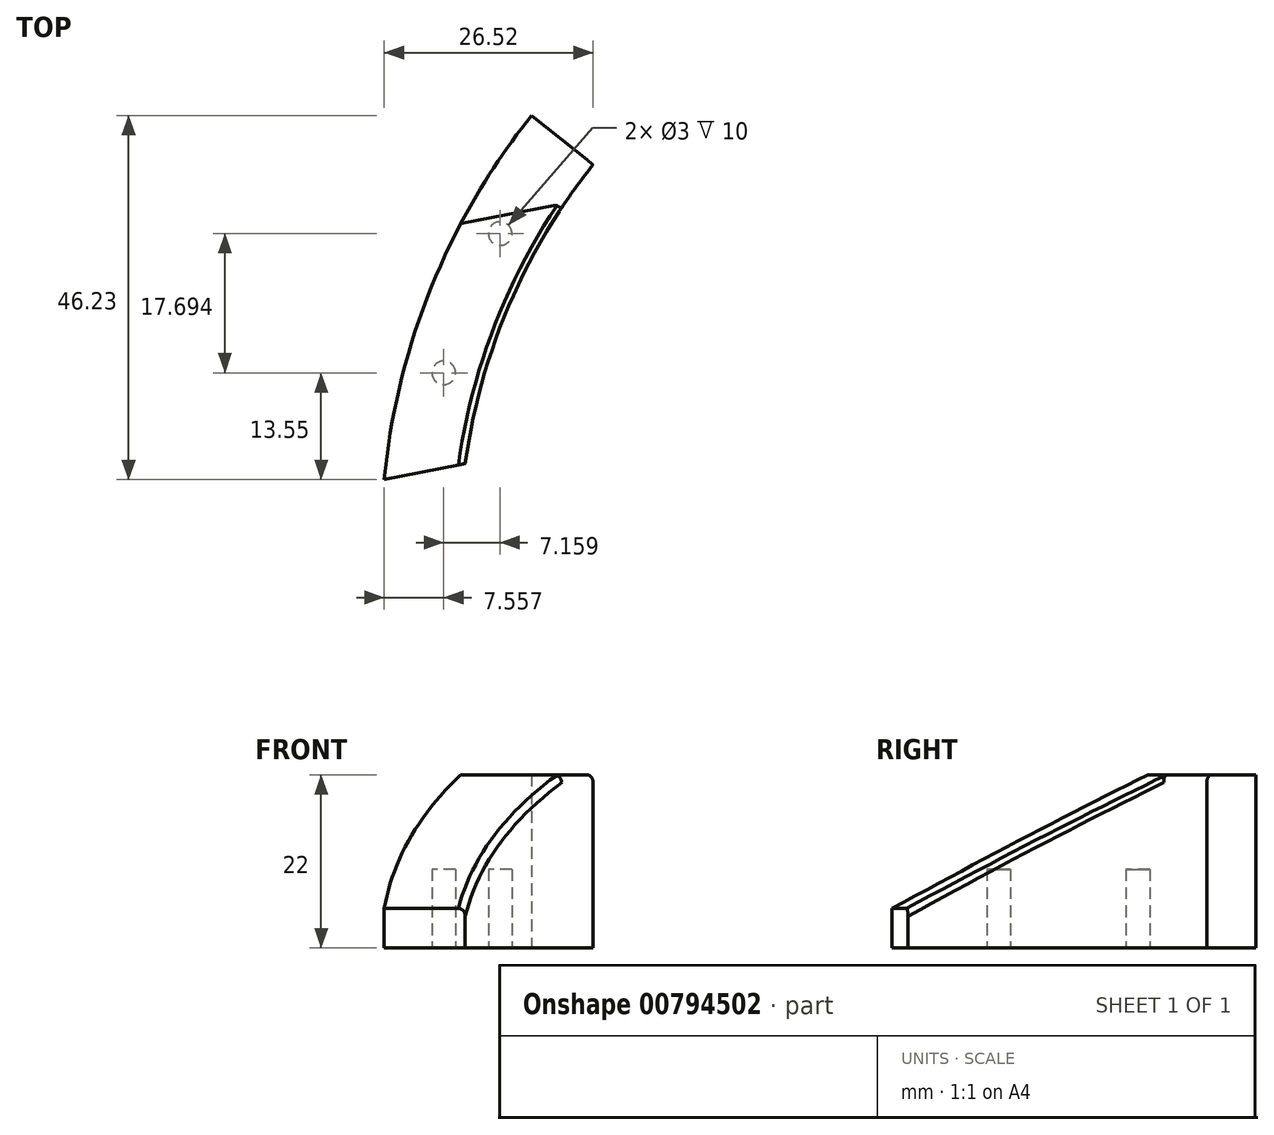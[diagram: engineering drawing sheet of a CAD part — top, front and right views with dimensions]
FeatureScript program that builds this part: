
annotation { "Feature Type Name" : "Feature", "Feature Type Description" : "" }
export const myFeature = defineFeature(function(context is Context, id is Id, definition is map)
    precondition{}
    {
        {
            var Q0;
            Q0=qCreatedBy(makeId("Top.planeOp"),FACE);
            var sketch = newSketch(context, id + "F0", { "sketchPlane" : qUnion([Q0])});
            skCircle(sketch, "E0", {"center": v(0, 0) * mm, "radius": 77.5 * mm});
            skCircle(sketch, "E1", {"center": v(0, 0) * mm, "radius": 76 * mm});
            skCircle(sketch, "E2", {"center": v(0, 0) * mm, "radius": 2.5 * mm});
            skLineSegment(sketch, "E3.bottom", {"start": v(0, 60) * mm, "end": v(-100, 60) * mm, "construction": true});
            skLineSegment(sketch, "E3.top", {"start": v(0, -60) * mm, "end": v(-100, -60) * mm, "construction": true});
            skLineSegment(sketch, "E3.left", {"start": v(0, 60) * mm, "end": v(0, -60) * mm, "construction": true});
            skLineSegment(sketch, "E3.right", {"start": v(-100, 60) * mm, "end": v(-100, -60) * mm, "construction": true});
            skCircle(sketch, "E4", {"center": v(0, 0) * mm, "radius": 87.5 * mm});
            skCircle(sketch, "E5", {"center": v(0, 0) * mm, "radius": 62.5 * mm});
            skLineSegment(sketch, "E6", {"start": v(0, 0) * mm, "end": v(-78.23, -94.42) * mm, "construction": true});
            skLineSegment(sketch, "E7", {"start": v(0, 0) * mm, "end": v(-84.15, 101.51) * mm, "construction": true});
            skLineSegment(sketch, "E8", {"start": v(0, 0) * mm, "end": v(-134.5, -26.47) * mm, "construction": true});
            skLineSegment(sketch, "E9", {"start": v(-85.85, -16.9) * mm, "end": v(-90.68, 7.63) * mm});
            skLineSegment(sketch, "E10", {"start": v(-90.68, 7.63) * mm, "end": v(-31.8, 19.22) * mm});
            skLineSegment(sketch, "E11", {"start": v(-31.8, 19.22) * mm, "end": v(-22.16, -29.84) * mm});
            skLineSegment(sketch, "E12", {"start": v(-22.16, -29.84) * mm, "end": v(-81.03, -41.42) * mm});
            skLineSegment(sketch, "E13", {"start": v(-90.68, 7.63) * mm, "end": v(-81.03, -41.42) * mm});
            skLineSegment(sketch, "E14.0", {"start": v(-84.8, 3.7) * mm, "end": v(-35.75, 13.35) * mm});
            skLineSegment(sketch, "E14.1", {"start": v(-84.8, 3.7) * mm, "end": v(-77.09, -35.55) * mm});
            skLineSegment(sketch, "E14.2", {"start": v(-28.03, -25.9) * mm, "end": v(-77.09, -35.55) * mm});
            skLineSegment(sketch, "E14.3", {"start": v(-35.75, 13.35) * mm, "end": v(-28.03, -25.9) * mm});
            skLineSegment(sketch, "E15.0", {"start": v(-94.2, 10) * mm, "end": v(-29.45, 22.74) * mm});
            skLineSegment(sketch, "E15.1", {"start": v(-94.2, 10) * mm, "end": v(-83.4, -44.95) * mm});
            skLineSegment(sketch, "E15.2", {"start": v(-18.63, -32.2) * mm, "end": v(-83.4, -44.95) * mm});
            skLineSegment(sketch, "E15.3", {"start": v(-29.45, 22.74) * mm, "end": v(-18.63, -32.2) * mm});
            skLineSegment(sketch, "E16", {"start": v(0, 0) * mm, "end": v(-75.25, 10.67) * mm, "construction": true});
            skLineSegment(sketch, "E17", {"start": v(-75.25, 10.67) * mm, "end": v(-86.63, 12.29) * mm});
            skLineSegment(sketch, "E18", {"start": v(-55.84, 67.36) * mm, "end": v(-48.5, 58.5) * mm});
            skLineSegment(sketch, "E19", {"start": v(0, 0) * mm, "end": v(-95.1, 63.54) * mm, "construction": true});
            skLineSegment(sketch, "E20", {"start": v(-72.76, 48.6) * mm, "end": v(-64.44, 43.05) * mm});
            skLineSegment(sketch, "E21", {"start": v(0, 0) * mm, "end": v(-81.95, 67.9) * mm, "construction": true});
            skLineSegment(sketch, "E22", {"start": v(-67.38, 55.83) * mm, "end": v(-59.68, 49.45) * mm});
            skLineSegment(sketch, "E23", {"start": v(0, 0) * mm, "end": v(-87.56, 69.86) * mm, "construction": true});
            skLineSegment(sketch, "E24", {"start": v(-60.58, 48.34) * mm, "end": v(-68.4, 54.57) * mm});
            skCircle(sketch, "E25", {"center": v(0, 0) * mm, "radius": 82.5 * mm, "construction": true});
            skCircle(sketch, "E26", {"center": v(-72.38, 39.58) * mm, "radius": 1.5 * mm});
            skCircle(sketch, "E27", {"center": v(-79.54, 21.89) * mm, "radius": 1.5 * mm});
            skSolve(sketch);
        }
        {
            var Q0;
            {var subQ0=sQuery(id+"F0.wireOp",EDGE,"E15.0");var subQ1=sQuery(id+"F0.wireOp",EDGE,"E0");var subQ2=makeQuery(id+"F0.imprint","INTERSECT",VERTEX,{"derivedFrom":[subQ1,subQ0]});Q0=makeQuery(id+"F0.imprint","IMPRINT",FACE,{"disambiguationData":[TD([[makeQuery(id+"F0.imprint","IMPRINT",EDGE,{"disambiguationData":[TD([[subQ2,-1.0]])],"derivedFrom":subQ1}),-1.0]])]});}
            var Q1;
            {var subQ5=sQuery(id+"F0.wireOp",EDGE,"E20");Q1=makeQuery(id+"F0.imprint","IMPRINT",FACE,{"disambiguationData":[TD([[makeQuery(id+"F0.imprint","IMPRINT",EDGE,{"derivedFrom":subQ5}),-1.0]])]});}
            var Q2;
            {var subQ0=sQuery(id+"F0.wireOp",EDGE,"E20");Q2=makeQuery(id+"F0.imprint","IMPRINT",FACE,{"disambiguationData":[TD([[makeQuery(id+"F0.imprint","IMPRINT",EDGE,{"derivedFrom":subQ0}),1.0]])]});}
            var Q3;
            {var subQ3=sQuery(id+"F0.wireOp",EDGE,"E17");var subQ7=sQuery(id+"F0.wireOp",EDGE,"E0");var subQ9=makeQuery(id+"F0.imprint","INTERSECT",VERTEX,{"derivedFrom":[subQ7,subQ3]});Q3=makeQuery(id+"F0.imprint","IMPRINT",FACE,{"disambiguationData":[TD([[makeQuery(id+"F0.imprint","IMPRINT",EDGE,{"disambiguationData":[TD([[subQ9,-1.0]])],"derivedFrom":subQ7}),-1.0]])]});}
            var Q4;
            {var subQ0=sQuery(id+"F0.wireOp",EDGE,"E17");var subQ1=sQuery(id+"F0.wireOp",EDGE,"E4");var subQ2=makeQuery(id+"F0.imprint","INTERSECT",VERTEX,{"derivedFrom":[subQ1,subQ0]});Q4=makeQuery(id+"F0.imprint","IMPRINT",FACE,{"disambiguationData":[TD([[makeQuery(id+"F0.imprint","IMPRINT",EDGE,{"disambiguationData":[TD([[subQ2,-1.0]])],"derivedFrom":subQ1}),1.0]])]});}
            var Q5;
            Q5=makeQuery(id+"F0.imprint","IMPRINT",FACE,{"disambiguationData":[TD([[makeQuery(id+"F0.imprint","IMPRINT",EDGE,{"derivedFrom":sQuery(id+"F0.wireOp",EDGE,"E26")}),1.0]])]});
            var Q6;
            Q6=makeQuery(id+"F0.imprint","IMPRINT",FACE,{"disambiguationData":[TD([[makeQuery(id+"F0.imprint","IMPRINT",EDGE,{"derivedFrom":sQuery(id+"F0.wireOp",EDGE,"E27")}),1.0]])]});
            extrude(context, id + "F1", {"entities" : qUnion([Q0, Q1, Q2, Q3, Q4, Q5, Q6]), "depth" : 22 * mm, "offsetDistance" : 25 * mm});
        }
        {
            var Q0;
            Q0=makeQuery(id+"F1.opExtrude","CAP_EDGE",EDGE,{"disambiguationData":[OSD([sQuery(id+"F0.wireOp",EDGE,"E17")])],"isStart":false});
            var Q1;
            Q1=makeQuery(id+"F1.opExtrude","CAP_EDGE",EDGE,{"disambiguationData":[OSD([sQuery(id+"F0.wireOp",EDGE,"E10")])],"isStart":false});
            chamfer(context, id + "F2", {"entities" : qUnion([Q0, Q1]), "chamferType" : ChamferType.TWO_OFFSETS, "width1" : 17 * mm, "oppositeDirection" : true, "width2" : 30 * mm, "tangentPropagation" : true});
        }
        {
            var Q0;
            Q0=makeQuery(id+"F0.imprint","IMPRINT",FACE,{"disambiguationData":[TD([[makeQuery(id+"F0.imprint","IMPRINT",EDGE,{"derivedFrom":sQuery(id+"F0.wireOp",EDGE,"E26")}),1.0]])]});
            var Q1;
            Q1=makeQuery(id+"F0.imprint","IMPRINT",FACE,{"disambiguationData":[TD([[makeQuery(id+"F0.imprint","IMPRINT",EDGE,{"derivedFrom":sQuery(id+"F0.wireOp",EDGE,"E27")}),1.0]])]});
            extrude(context, id + "F3", {"entities" : qUnion([Q0, Q1]), "operationType" : NewBodyOperationType.REMOVE, "depth" : 10 * mm, "offsetDistance" : 25 * mm});
        }
        {
            var Q0;
            Q0=makeQuery(id+"F2.opChamfer","BLEND_EDGE",EDGE,{"blendedFrom":[makeQuery(id+"F1.opExtrude","CAP_EDGE",EDGE,{"disambiguationData":[OSD([sQuery(id+"F0.wireOp",EDGE,"E10")])],"isStart":false}),makeQuery(id+"F1.opExtrude","SWEPT_FACE",FACE,{"disambiguationData":[OSD([sQuery(id+"F0.wireOp",EDGE,"E0")])]})],"blendedInto":[makeQuery(id+"F1.opExtrude","SWEPT_FACE",FACE,{"disambiguationData":[OSD([sQuery(id+"F0.wireOp",EDGE,"E0")])]})]});
            var Q1;
            Q1=makeQuery(id+"F1.opExtrude","CAP_EDGE",EDGE,{"disambiguationData":[OSD([sQuery(id+"F0.wireOp",EDGE,"E0")])],"isStart":false});
            fillet(context, id + "F4", {"entities" : qUnion([Q0, Q1]), "radius" : 1 * mm, "tangentPropagation" : true, "allowEdgeOverflow" : false});
        }
    });
